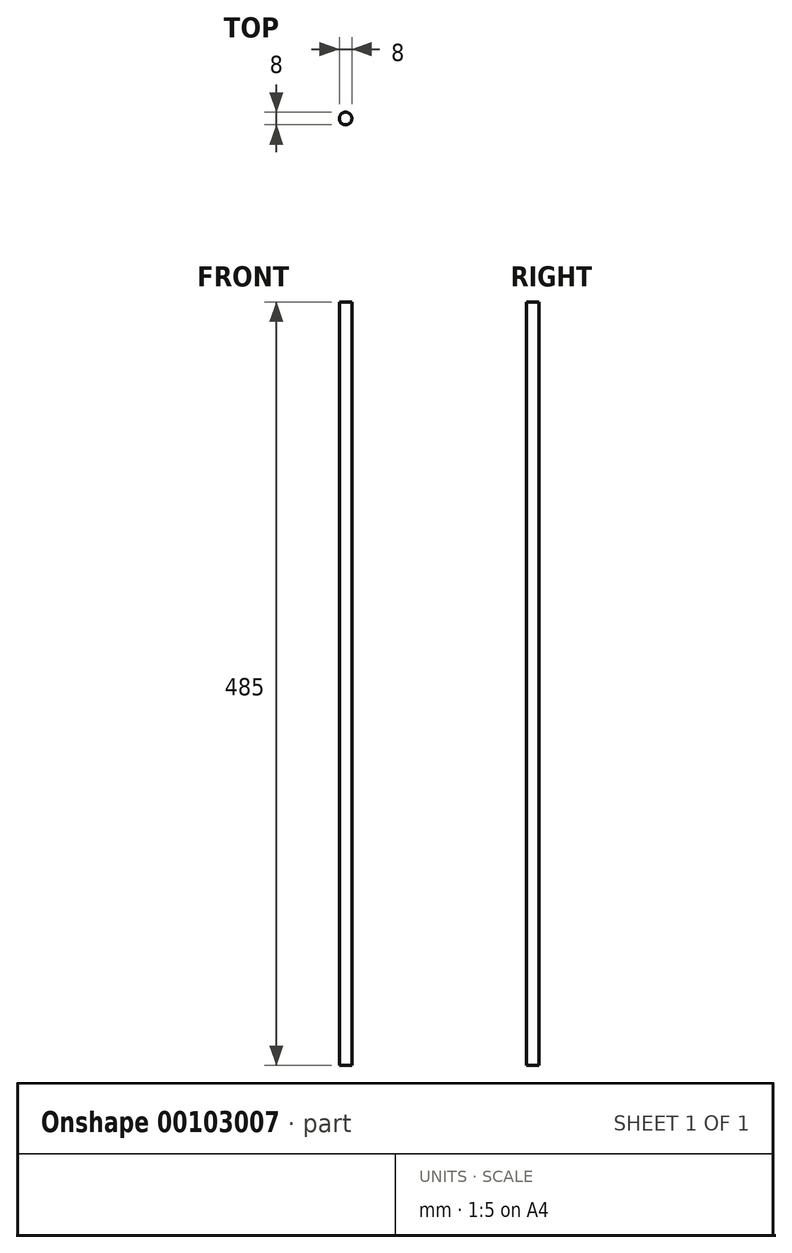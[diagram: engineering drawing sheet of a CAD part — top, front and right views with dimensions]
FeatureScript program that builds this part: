
annotation { "Feature Type Name" : "Feature", "Feature Type Description" : "" }
export const myFeature = defineFeature(function(context is Context, id is Id, definition is map)
    precondition{}
    {
        {
            var Q0;
            Q0=qCreatedBy(makeId("Top.planeOp"),FACE);
            var sketch = newSketch(context, id + "F0", { "sketchPlane" : qUnion([Q0])});
            skCircle(sketch, "E0", {"center": v(0, 0) * mm, "radius": 4 * mm});
            skSolve(sketch);
        }
        {
            var Q0;
            Q0=qSketchRegion(id+"F0",true);
            extrude(context, id + "F1", {"entities" : qUnion([Q0]), "depth" : 485 * mm});
        }
    });
